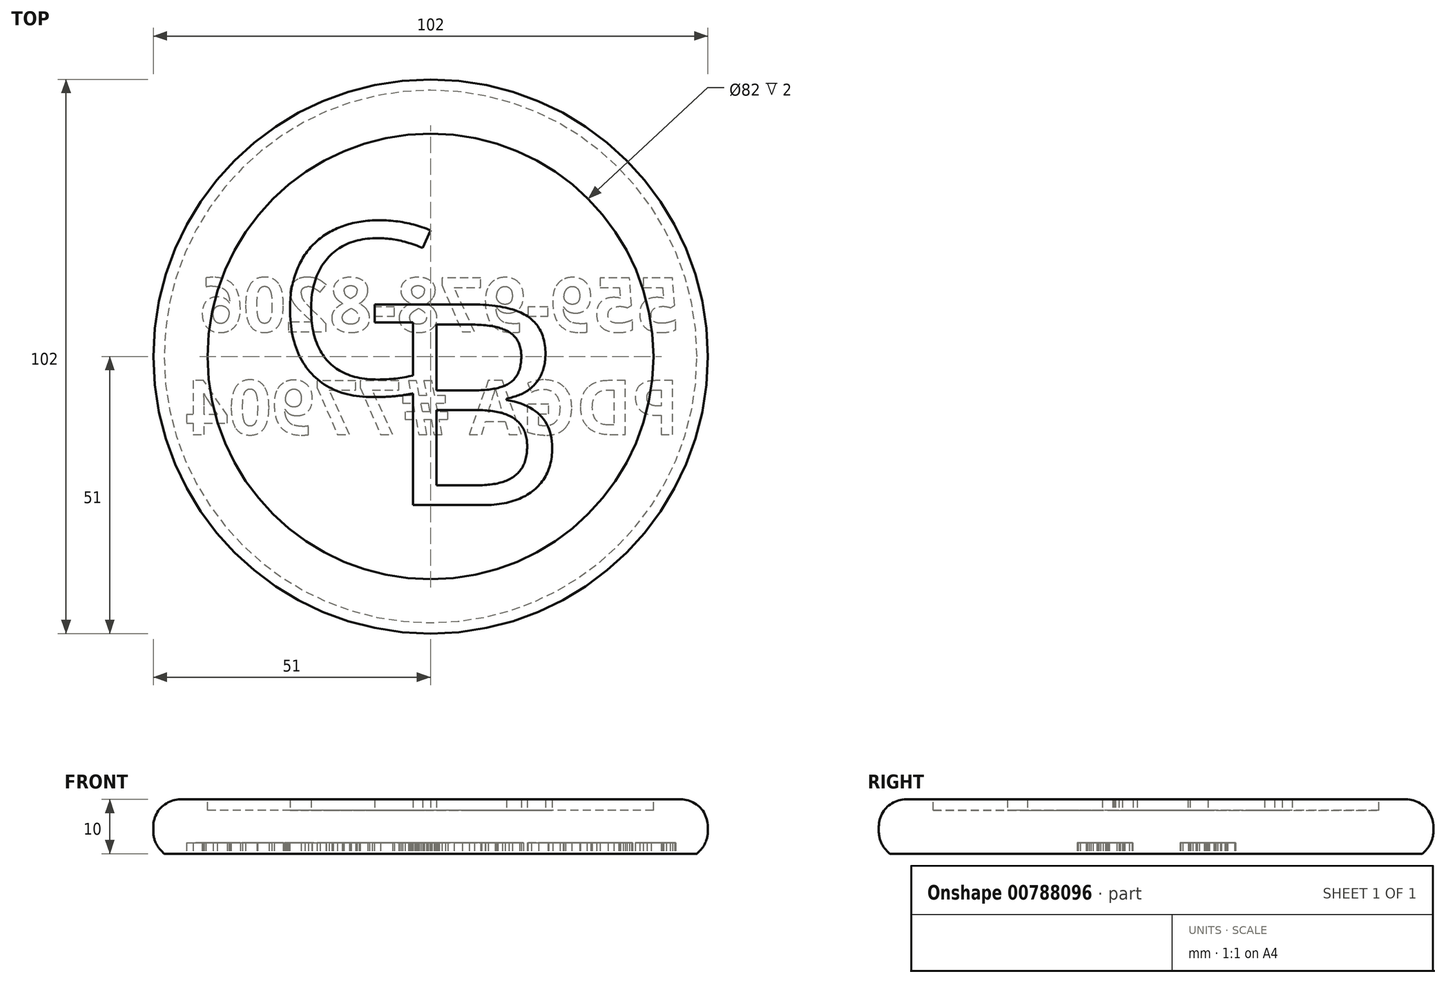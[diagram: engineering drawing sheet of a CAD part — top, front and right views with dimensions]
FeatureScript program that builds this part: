
annotation { "Feature Type Name" : "Feature", "Feature Type Description" : "" }
export const myFeature = defineFeature(function(context is Context, id is Id, definition is map)
    precondition{}
    {
        {
            var Q0;
            Q0=qCreatedBy(makeId("Top.planeOp"),FACE);
            var sketch = newSketch(context, id + "F0", { "sketchPlane" : qUnion([Q0])});
            skCircle(sketch, "E0", {"center": v(0, 0) * mm, "radius": 51 * mm});
            skSolve(sketch);
        }
        {
            var Q0;
            Q0=makeQuery(id+"F0.imprint","IMPRINT",FACE,{"disambiguationData":[TD([[makeQuery(id+"F0.imprint","IMPRINT",EDGE,{"derivedFrom":sQuery(id+"F0.wireOp",EDGE,"E0")}),1.0]])]});
            extrude(context, id + "F1", {"entities" : qUnion([Q0]), "depth" : 10 * mm, "offsetDistance" : 25 * mm});
        }
        {
            var Q0;
            Q0=makeQuery(id+"F1.opExtrude","CAP_FACE",FACE,{"disambiguationData":[OSD([sQuery(id+"F0.wireOp",EDGE,"E0")])],"isStart":false});
            var sketch = newSketch(context, id + "F2", { "sketchPlane" : qUnion([Q0])});
            skCircle(sketch, "E1", {"center": v(0, 0) * mm, "radius": 41 * mm});
            skSolve(sketch);
        }
        {
            var Q0;
            Q0=makeQuery(id+"F2.imprint","IMPRINT",FACE,{"disambiguationData":[TD([[makeQuery(id+"F2.imprint","IMPRINT",EDGE,{"derivedFrom":sQuery(id+"F2.wireOp",EDGE,"E1")}),1.0]])]});
            extrude(context, id + "F3", {"entities" : qUnion([Q0]), "operationType" : NewBodyOperationType.REMOVE, "oppositeDirection" : true, "depth" : 2 * mm, "offsetDistance" : 25 * mm});
        }
        {
            var Q0;
            Q0=makeQuery(id+"F3.boolean.opBoolean","COPY",FACE,{"derivedFrom":makeQuery(id+"F3.opExtrude","CAP_FACE",FACE,{"disambiguationData":[OSD([sQuery(id+"F2.wireOp",EDGE,"E1")])],"isStart":false})});
            var sketch = newSketch(context, id + "F4", { "sketchPlane" : qUnion([Q0])});
            skText(sketch, "E2", { "text": "G", "fontName": "OpenSans-Regular.ttf"});
            skText(sketch, "E3", { "text": "B", "fontName": "OpenSans-Regular.ttf"});
            const initialGuessF4  = {"E2": [-0.02857, -0.00704, 1, 0, 0.03193], "E3": [-0.0083, -0.02735, 1, 0, 0.03725]};
            skSetInitialGuess(sketch, initialGuessF4);
            skSolve(sketch);
        }
        {
            var Q0;
            Q0 = qSketchRegion(id + "F4", true);
            extrude(context, id + "F5", {"entities" : qUnion([Q0]), "operationType" : NewBodyOperationType.ADD, "depth" : 2 * mm, "offsetDistance" : 25 * mm});
        }
        {
            var Q0;
            Q0=makeQuery(id+"F1.opExtrude","CAP_EDGE",EDGE,{"disambiguationData":[OSD([sQuery(id+"F0.wireOp",EDGE,"E0")])],"isStart":false});
            fillet(context, id + "F6", {"entities" : qUnion([Q0]), "radius" : 5 * mm, "tangentPropagation" : true, "allowEdgeOverflow" : false});
        }
        {
            var Q0;
            Q0=makeQuery(id+"F1.opExtrude","CAP_EDGE",EDGE,{"disambiguationData":[OSD([sQuery(id+"F0.wireOp",EDGE,"E0")])],"isStart":true});
            chamfer(context, id + "F7", {"entities" : qUnion([Q0]), "width" : 2 * mm, "tangentPropagation" : true});
        }
        {
            var Q0;
            {var subQ0=sQuery(id+"F0.wireOp",EDGE,"E0");Q0=makeQuery(id+"F7.opChamfer","BLEND_EDGE",EDGE,{"blendedFrom":[makeQuery(id+"F1.opExtrude","CAP_EDGE",EDGE,{"disambiguationData":[OSD([subQ0])],"isStart":true}),makeQuery(id+"F1.opExtrude","SWEPT_FACE",FACE,{"disambiguationData":[OSD([subQ0])]})],"blendedInto":[makeQuery(id+"F1.opExtrude","SWEPT_FACE",FACE,{"disambiguationData":[OSD([subQ0])]})]});}
            fillet(context, id + "F8", {"entities" : qUnion([Q0]), "radius" : 5 * mm, "tangentPropagation" : true, "allowEdgeOverflow" : false});
        }
        {
            var Q0;
            Q0=makeQuery(id+"F1.opExtrude","CAP_FACE",FACE,{"disambiguationData":[OSD([sQuery(id+"F0.wireOp",EDGE,"E0")])],"isStart":true});
            var sketch = newSketch(context, id + "F9", { "sketchPlane" : qUnion([Q0])});
            skText(sketch, "E4", { "text": "559-978-8206\nPDGA #77904", "fontName": "OpenSans-Bold.ttf"});
            const initialGuessF9  = {"E4": [0.04577, -0.00454, -1, 0, 0.01]};
            skSetInitialGuess(sketch, initialGuessF9);
            skSolve(sketch);
        }
        {
            var Q0;
            Q0 = qSketchRegion(id + "F9", true);
            extrude(context, id + "F10", {"entities" : qUnion([Q0]), "operationType" : NewBodyOperationType.REMOVE, "oppositeDirection" : true, "depth" : 2 * mm, "offsetDistance" : 25 * mm});
        }
    });
